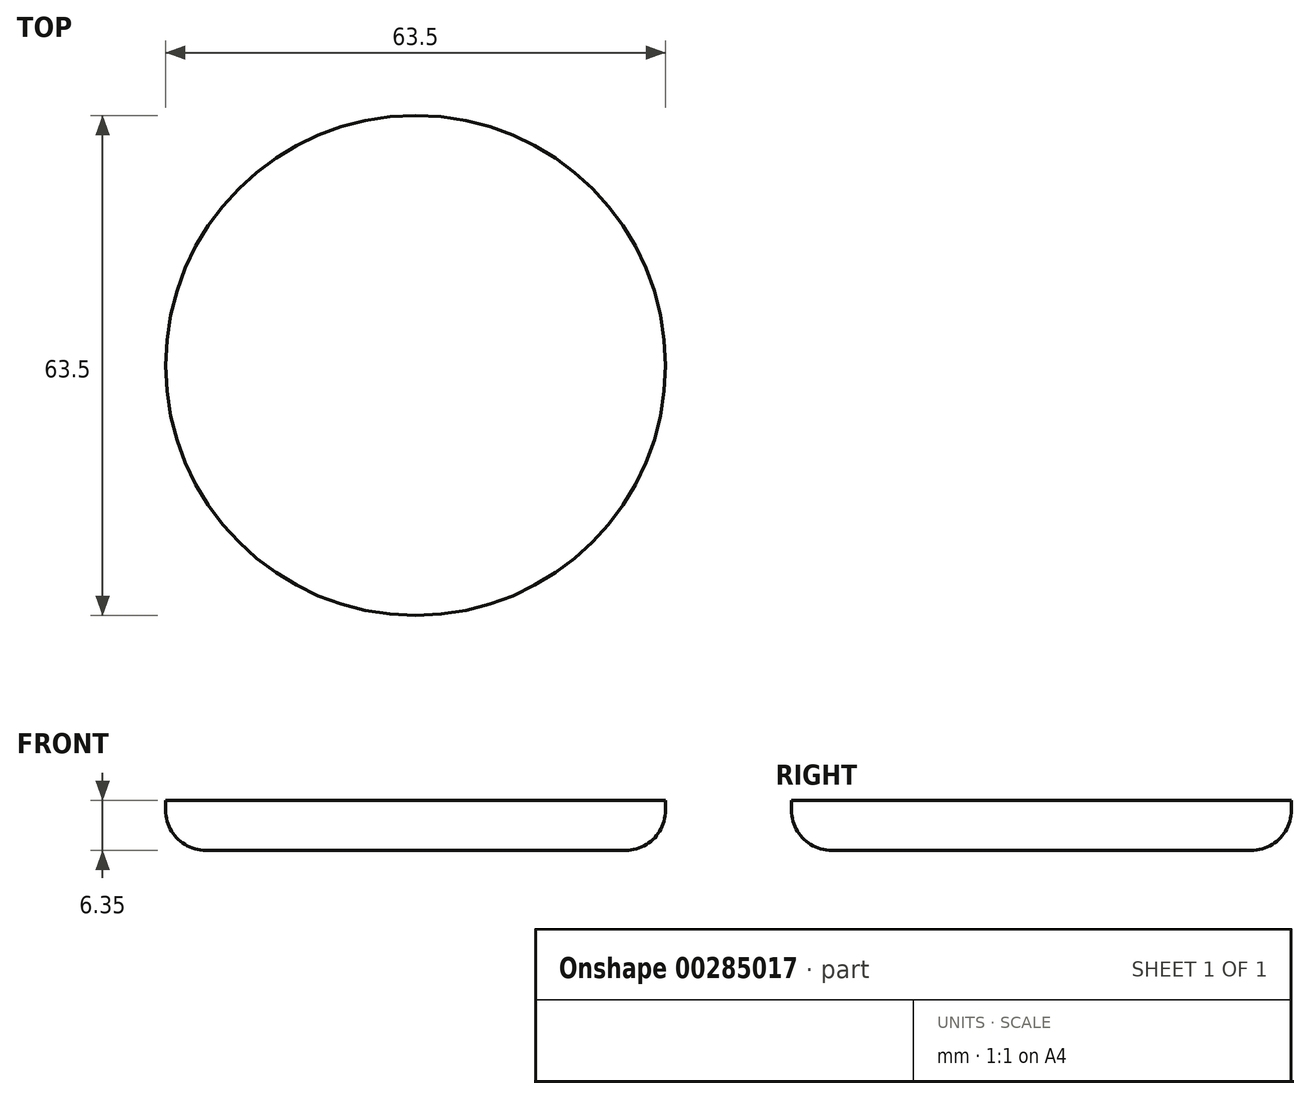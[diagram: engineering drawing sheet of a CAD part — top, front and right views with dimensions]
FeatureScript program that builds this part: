
annotation { "Feature Type Name" : "Feature", "Feature Type Description" : "" }
export const myFeature = defineFeature(function(context is Context, id is Id, definition is map)
    precondition{}
    {
        {
            var Q0;
            Q0=qCreatedBy(makeId("Top.planeOp"),FACE);
            var sketch = newSketch(context, id + "F0", { "sketchPlane" : qUnion([Q0])});
            skCircle(sketch, "E0", {"center": v(-67.7, 30.8) * mm, "radius": 31.75 * mm});
            skSolve(sketch);
        }
        {
            var Q0;
            Q0=makeQuery(id+"F0.imprint","IMPRINT",FACE,{"disambiguationData":[TD([[makeQuery(id+"F0.imprint","IMPRINT",EDGE,{"derivedFrom":sQuery(id+"F0.wireOp",EDGE,"E0")}),1.0]])]});
            extrude(context, id + "F1", {"entities" : qUnion([Q0]), "depth" : 6.35 * mm});
        }
        {
            var Q0;
            Q0=makeQuery(id+"F1.opExtrude","CAP_FACE",FACE,{"disambiguationData":[OSD([sQuery(id+"F0.wireOp",EDGE,"E0")])],"isStart":true});
            fillet(context, id + "F2", {"entities" : qUnion([Q0]), "radius" : 5.08 * mm, "tangentPropagation" : true, "allowEdgeOverflow" : false});
        }
    });
